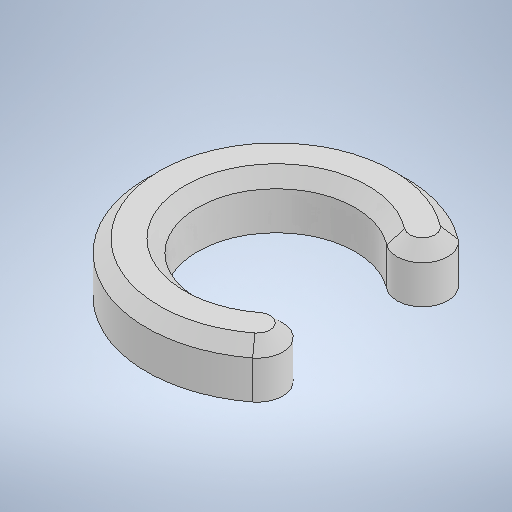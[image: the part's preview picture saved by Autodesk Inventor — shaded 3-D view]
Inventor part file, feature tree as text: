
AUTODESK INVENTOR PART (.ipt)
format: ipt  version: 2025.2 (Build 292293000, 293)  size: 254,464 bytes
history: native  units: mm
features: extrude x1, chamfer x1, sketch x1
ambient origin geometry x8: Origin, YZ Plane, XZ Plane, XY Plane, X Axis, Y Axis, Z Axis, Center Point
bodies: Solid1 (feature_tree)
feature tree (3):
  extrude  "Extrusion1"  Depth=2.0mm
  chamfer  "Chamfer1"  Distance=2.5mm
  sketch  "Sketch1"  dims[d0=6.2mm d1=2.0mm d3=2.5mm d4=2.0mm d5=0.0mm d6=0.5mm d7=2.0mm d8=45.0deg]
